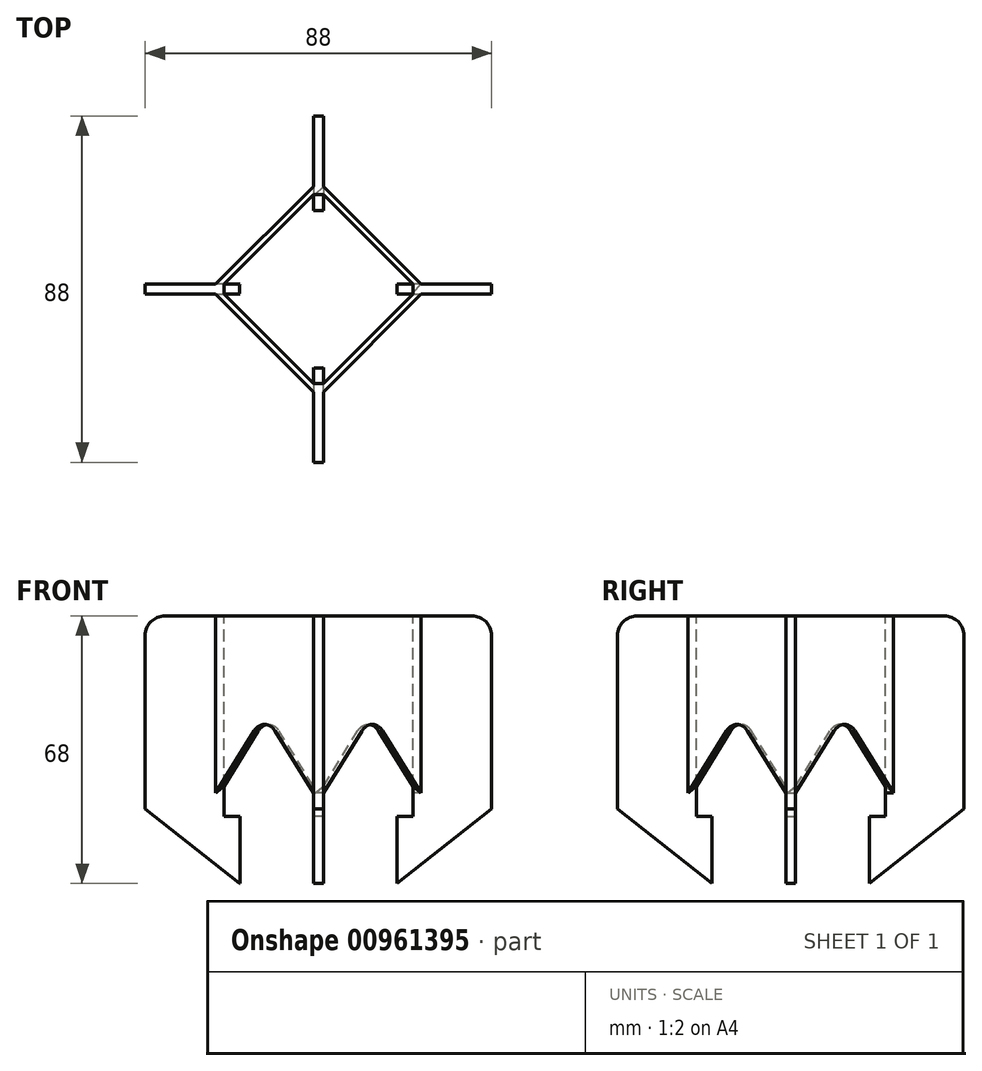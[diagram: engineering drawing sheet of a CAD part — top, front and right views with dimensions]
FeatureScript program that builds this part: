
annotation { "Feature Type Name" : "Feature", "Feature Type Description" : "" }
export const myFeature = defineFeature(function(context is Context, id is Id, definition is map)
    precondition{}
    {
        {
            var Q0;
            Q0=qCreatedBy(makeId("Front.planeOp"),FACE);
            var sketch = newSketch(context, id + "F0", { "sketchPlane" : qUnion([Q0])});
            skLineSegment(sketch, "E0", {"start": v(0, 0) * mm, "end": v(0, 17) * mm});
            skLineSegment(sketch, "E1", {"start": v(0, 17) * mm, "end": v(4, 17) * mm});
            skLineSegment(sketch, "E2", {"start": v(4, 17) * mm, "end": v(4, 68) * mm});
            skLineSegment(sketch, "E3", {"start": v(4, 68) * mm, "end": v(19, 68) * mm});
            skLineSegment(sketch, "E4", {"start": v(24, 63) * mm, "end": v(24, 19) * mm});
            skLineSegment(sketch, "E5", {"start": v(24, 19) * mm, "end": v(0, 0) * mm});
            skPoint(sketch, "E6.visualSharp", {"position": v(24, 68) * mm});
            skArc(sketch, "E6.filletArc", {"start": v(24, 63) * mm, "mid": v(22.54, 66.54) * mm, "end": v(19, 68) * mm});
            skSolve(sketch);
        }
        {
            var Q0;
            Q0=makeQuery(id+"F0.imprint","IMPRINT",FACE,{"disambiguationData":[TD([[makeQuery(id+"F0.imprint","IMPRINT",EDGE,{"derivedFrom":sQuery(id+"F0.wireOp",EDGE,"E0")}),-1.0]])]});
            extrude(context, id + "F1", {"entities" : qUnion([Q0]), "endBound" : BoundingType.SYMMETRIC, "depth" : 2.5 * mm, "offsetDistance" : 25 * mm});
        }
        {
            var Q0;
            Q0=makeQuery(id+"F0.imprint","IMPRINT",FACE,{"disambiguationData":[TD([[makeQuery(id+"F0.imprint","IMPRINT",EDGE,{"derivedFrom":sQuery(id+"F0.wireOp",EDGE,"E0")}),-1.0]])]});
            var sketch = newSketch(context, id + "F2", { "sketchPlane" : qUnion([Q0])});
            skLineSegment(sketch, "E7", {"start": v(0, 0) * mm, "end": v(-20, 0) * mm});
            skLineSegment(sketch, "E8", {"start": v(-20, 0) * mm, "end": v(-20, 8.1) * mm});
            skSolve(sketch);
        }
        {
            var Q0;
            Q0=makeQuery(id+"F1.opExtrude","SWEPT_BODY",BODY,{"disambiguationData":[OSD([sQuery(id+"F0.wireOp",EDGE,"E0"),sQuery(id+"F0.wireOp",EDGE,"E1"),sQuery(id+"F0.wireOp",EDGE,"E2"),sQuery(id+"F0.wireOp",EDGE,"E3"),sQuery(id+"F0.wireOp",EDGE,"E4"),sQuery(id+"F0.wireOp",EDGE,"E5"),sQuery(id+"F0.wireOp",EDGE,"E6.filletArc")])]});
            var Q1;
            Q1=sQuery(id+"F2.wireOp",EDGE,"E8");
            circularPattern(context, id + "F3", {"entities" : qUnion([Q0]), "axis" : qUnion([Q1]), "angle" : 360 * degree, "instanceCount" : 4, "equalSpace" : true});
        }
        {
            var Q0;
            Q0=makeQuery(id+"F3.opPattern","COPY",FACE,{"derivedFrom":makeQuery(id+"F1.opExtrude","SWEPT_FACE",FACE,{"disambiguationData":[OSD([sQuery(id+"F0.wireOp",EDGE,"E3")])]}),"instanceName":"1"});
            var sketch = newSketch(context, id + "F4", { "sketchPlane" : qUnion([Q0])});
            skPoint(sketch, "E9.0", {"position": v(-20, 20) * mm});
            skPoint(sketch, "E10.0", {"position": v(-40, 0) * mm});
            skPoint(sketch, "E11.0", {"position": v(0, 0) * mm});
            skPoint(sketch, "E12.0", {"position": v(-20, -20) * mm});
            skCircle(sketch, "E13", {"center": v(-20, 0) * mm, "radius": 20 * mm});
            skSolve(sketch);
        }
        {
            var Q0;
            Q0=makeQuery(id+"F1.opExtrude","SWEPT_FACE",FACE,{"disambiguationData":[OSD([sQuery(id+"F0.wireOp",EDGE,"E3")])]});
            var sketch = newSketch(context, id + "F5", { "sketchPlane" : qUnion([Q0])});
            skPoint(sketch, "E14.0.3.end.orphan", {"position": v(19, 1.25) * mm});
            skPoint(sketch, "E14.0.2.end.orphan", {"position": v(19, -1.25) * mm});
            skPoint(sketch, "E14.0.1.end.orphan", {"position": v(4, -1.25) * mm});
            skPoint(sketch, "E15.0.1.start.orphan", {"position": v(-21.25, 24) * mm});
            skPoint(sketch, "E15.0.3.end.orphan", {"position": v(-21.25, 39) * mm});
            skPoint(sketch, "E15.0.3.start.orphan", {"position": v(-18.75, 39) * mm});
            skLineSegment(sketch, "E16.0.2", {"start": v(-18.75, 24) * mm, "end": v(-18.75, 26.12) * mm});
            skLineSegment(sketch, "E17.0.0", {"start": v(6.12, 1.25) * mm, "end": v(4, 1.25) * mm});
            skLineSegment(sketch, "E18", {"start": v(-18.75, 24) * mm, "end": v(4, 1.25) * mm});
            skLineSegment(sketch, "E19.0", {"start": v(-18.75, 26.12) * mm, "end": v(6.12, 1.25) * mm});
            skSolve(sketch);
        }
        {
            var Q0;
            Q0 = qSketchRegion(id + "F5", true);
            extrude(context, id + "F6", {"entities" : qUnion([Q0]), "oppositeDirection" : true, "depth" : 45 * mm, "offsetDistance" : 25 * mm});
        }
        {
            var Q0;
            Q0=makeQuery(id+"F6.opExtrude","SWEPT_FACE",FACE,{"disambiguationData":[OSD([sQuery(id+"F5.wireOp",EDGE,"E19.0")])]});
            var sketch = newSketch(context, id + "F7", { "sketchPlane" : qUnion([Q0])});
            skLineSegment(sketch, "E20", {"start": v(17.9, 38.73) * mm, "end": v(31.73, 23) * mm});
            skLineSegment(sketch, "E21", {"start": v(10.39, 38.73) * mm, "end": v(-3.44, 23) * mm});
            skPoint(sketch, "E22.visualSharp", {"position": v(14.14, 43) * mm});
            skArc(sketch, "E22.filletArc", {"start": v(17.9, 38.73) * mm, "mid": v(14.14, 40.43) * mm, "end": v(10.39, 38.73) * mm});
            skSolve(sketch);
        }
        {
            var Q0;
            Q0=makeQuery(id+"F7.imprint","IMPRINT",FACE,{"disambiguationData":[TD([[makeQuery(id+"F7.imprint","IMPRINT",EDGE,{"derivedFrom":sQuery(id+"F7.wireOp",EDGE,"E20")}),-1.0]])]});
            extrude(context, id + "F8", {"entities" : qUnion([Q0]), "operationType" : NewBodyOperationType.REMOVE, "oppositeDirection" : true, "depth" : 5 * mm, "offsetDistance" : 25 * mm});
        }
        {
            var Q0;
            Q0=makeQuery(id+"F6.opExtrude","SWEPT_BODY",BODY,{"disambiguationData":[OSD([sQuery(id+"F5.wireOp",EDGE,"E16.0.2"),sQuery(id+"F5.wireOp",EDGE,"E17.0.0"),sQuery(id+"F5.wireOp",EDGE,"E18"),sQuery(id+"F5.wireOp",EDGE,"E19.0")])]});
            var Q1;
            Q1=sQuery(id+"F4.wireOp",EDGE,"E13");
            circularPattern(context, id + "F9", {"operationType" : NewBodyOperationType.ADD, "entities" : qUnion([Q0]), "axis" : qUnion([Q1]), "angle" : 360 * degree, "instanceCount" : 4, "equalSpace" : true});
        }
        {
            var Q0;
            Q0=makeQuery(id+"F3.opPattern","COPY",FACE,{"derivedFrom":makeQuery(id+"F1.opExtrude","SWEPT_FACE",FACE,{"disambiguationData":[OSD([sQuery(id+"F0.wireOp",EDGE,"E1")])]}),"instanceName":"1"});
            var sketch = newSketch(context, id + "F10", { "sketchPlane" : qUnion([Q0])});
            skPoint(sketch, "E23.0", {"position": v(-20, 20) * mm});
            skPoint(sketch, "E24.0", {"position": v(-20, -20) * mm});
            skPoint(sketch, "E25.0", {"position": v(-40, 0) * mm});
            skPoint(sketch, "E26.0", {"position": v(0, 0) * mm});
            skLineSegment(sketch, "E27.0", {"start": v(-18.75, 20) * mm, "end": v(-21.25, 20) * mm});
            skLineSegment(sketch, "E28.0", {"start": v(0, -1.25) * mm, "end": v(0, 1.25) * mm});
            skLineSegment(sketch, "E29.0", {"start": v(-21.25, -20) * mm, "end": v(-18.75, -20) * mm});
            skPoint(sketch, "E30.0", {"position": v(-40, 1.25) * mm});
            skLineSegment(sketch, "E31.0", {"start": v(-40, 1.25) * mm, "end": v(-40, -1.25) * mm});
            skArc(sketch, "E32", {"start": v(-39.96, 1.25) * mm, "mid": v(-40, 0) * mm, "end": v(-39.96, -1.25) * mm});
            skLineSegment(sketch, "E33", {"start": v(-21.25, 20) * mm, "end": v(-21.25, 19.96) * mm});
            skLineSegment(sketch, "E34", {"start": v(-18.75, 20) * mm, "end": v(-18.75, 19.96) * mm});
            skLineSegment(sketch, "E35", {"start": v(0, 1.25) * mm, "end": v(-0.04, 1.25) * mm});
            skLineSegment(sketch, "E36", {"start": v(0, -1.25) * mm, "end": v(-0.04, -1.25) * mm});
            skLineSegment(sketch, "E37", {"start": v(-21.25, -20) * mm, "end": v(-21.25, -19.96) * mm});
            skLineSegment(sketch, "E38", {"start": v(-18.75, -20) * mm, "end": v(-18.75, -19.96) * mm});
            skLineSegment(sketch, "E39", {"start": v(-40, -1.25) * mm, "end": v(-39.96, -1.25) * mm});
            skLineSegment(sketch, "E40", {"start": v(-40, 1.25) * mm, "end": v(-39.96, 1.25) * mm});
            skArc(sketch, "E41.trimOffspring", {"start": v(-21.25, -19.96) * mm, "mid": v(-20, -20) * mm, "end": v(-18.75, -19.96) * mm});
            skArc(sketch, "E42.trimOffspring", {"start": v(-18.75, 19.96) * mm, "mid": v(-20, 20) * mm, "end": v(-21.25, 19.96) * mm});
            skArc(sketch, "E43.trimOffspring", {"start": v(-0.04, -1.25) * mm, "mid": v(0, 0) * mm, "end": v(-0.04, 1.25) * mm});
            skSolve(sketch);
        }
        {
            var Q0;
            Q0 = qSketchRegion(id + "F10", true);
            extrude(context, id + "F11", {"entities" : qUnion([Q0]), "operationType" : NewBodyOperationType.ADD, "oppositeDirection" : true, "depth" : 17 * mm, "offsetDistance" : 25 * mm});
        }
    });
